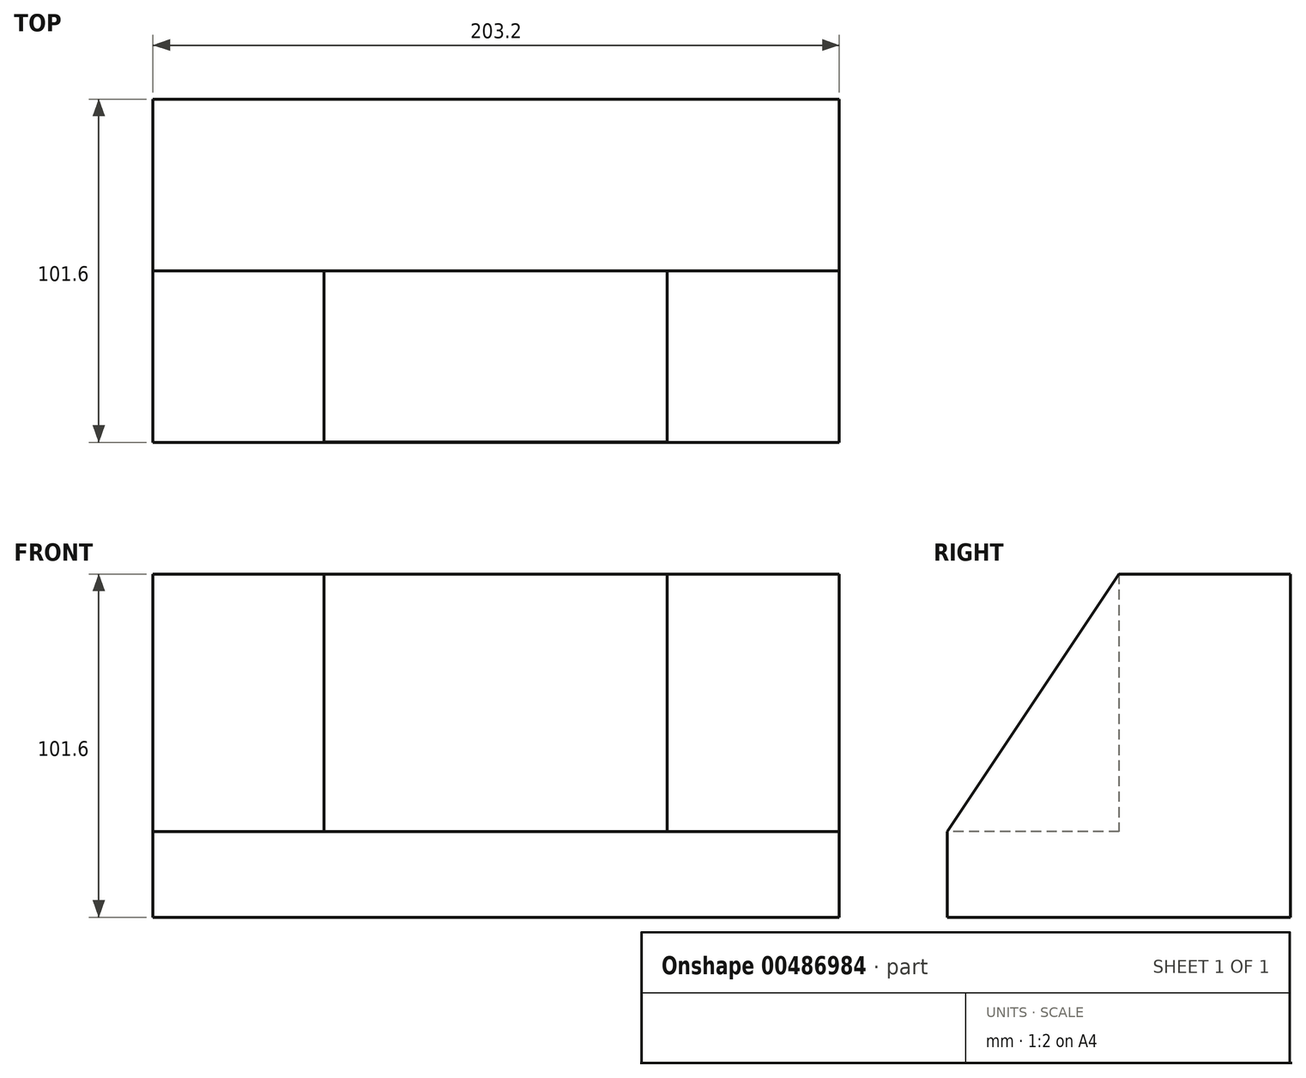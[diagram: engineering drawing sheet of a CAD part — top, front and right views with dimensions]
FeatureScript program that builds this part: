
annotation { "Feature Type Name" : "Feature", "Feature Type Description" : "" }
export const myFeature = defineFeature(function(context is Context, id is Id, definition is map)
    precondition{}
    {
        {
            var Q0;
            Q0=qCreatedBy(makeId("Front.planeOp"),FACE);
            var sketch = newSketch(context, id + "F0", { "sketchPlane" : qUnion([Q0])});
            skLineSegment(sketch, "E0.bottom", {"start": v(-109.3, 35.82) * mm, "end": v(93.9, 35.82) * mm});
            skLineSegment(sketch, "E0.top", {"start": v(-109.3, -65.78) * mm, "end": v(93.9, -65.78) * mm});
            skLineSegment(sketch, "E0.left", {"start": v(-109.3, 35.82) * mm, "end": v(-109.3, -65.78) * mm});
            skLineSegment(sketch, "E0.right", {"start": v(93.9, 35.82) * mm, "end": v(93.9, -65.78) * mm});
            skSolve(sketch);
        }
        {
            var Q0;
            Q0 = qSketchRegion(id + "F0", true);
            extrude(context, id + "F1", {"entities" : qUnion([Q0]), "depth" : 101.6 * mm});
        }
        {
            var Q0;
            Q0=makeQuery(id+"F1.opExtrude","CAP_FACE",FACE,{"disambiguationData":[OSD([sQuery(id+"F0.wireOp",EDGE,"E0.bottom"),sQuery(id+"F0.wireOp",EDGE,"E0.top"),sQuery(id+"F0.wireOp",EDGE,"E0.left"),sQuery(id+"F0.wireOp",EDGE,"E0.right")])],"isStart":false});
            var sketch = newSketch(context, id + "F2", { "sketchPlane" : qUnion([Q0])});
            skLineSegment(sketch, "E1", {"start": v(-109.3, 35.82) * mm, "end": v(-58.63, 35.82) * mm});
            skLineSegment(sketch, "E2.bottom", {"start": v(-58.63, 35.82) * mm, "end": v(42.97, 35.82) * mm});
            skLineSegment(sketch, "E2.top", {"start": v(-58.63, -40.38) * mm, "end": v(42.97, -40.38) * mm});
            skLineSegment(sketch, "E2.left", {"start": v(-58.63, 35.82) * mm, "end": v(-58.63, -40.38) * mm});
            skLineSegment(sketch, "E2.right", {"start": v(42.97, 35.82) * mm, "end": v(42.97, -40.38) * mm});
            skSolve(sketch);
        }
        {
            var Q0;
            Q0 = qSketchRegion(id + "F2", true);
            extrude(context, id + "F3", {"entities" : qUnion([Q0]), "operationType" : NewBodyOperationType.REMOVE, "oppositeDirection" : true, "depth" : 50.8 * mm});
        }
        {
            var Q0;
            Q0=makeQuery(id+"F1.opExtrude","SWEPT_FACE",FACE,{"disambiguationData":[OSD([sQuery(id+"F0.wireOp",EDGE,"E0.left")])]});
            var sketch = newSketch(context, id + "F4", { "sketchPlane" : qUnion([Q0])});
            skLineSegment(sketch, "E3", {"start": v(101.6, -65.78) * mm, "end": v(101.6, -40.38) * mm});
            skLineSegment(sketch, "E4", {"start": v(101.6, -40.38) * mm, "end": v(101.6, 35.82) * mm});
            skLineSegment(sketch, "E5", {"start": v(101.6, 35.82) * mm, "end": v(50.8, 35.82) * mm});
            skLineSegment(sketch, "E6", {"start": v(50.8, 35.82) * mm, "end": v(101.6, -40.38) * mm});
            skSolve(sketch);
        }
        {
            var Q0;
            Q0 = qSketchRegion(id + "F4", true);
            extrude(context, id + "F5", {"entities" : qUnion([Q0]), "operationType" : NewBodyOperationType.REMOVE, "oppositeDirection" : true, "depth" : 50.8 * mm});
        }
        {
            var Q0;
            Q0=makeQuery(id+"F1.opExtrude","SWEPT_FACE",FACE,{"disambiguationData":[OSD([sQuery(id+"F0.wireOp",EDGE,"E0.right")])]});
            var sketch = newSketch(context, id + "F6", { "sketchPlane" : qUnion([Q0])});
            skLineSegment(sketch, "E7", {"start": v(-101.6, -65.78) * mm, "end": v(-101.6, -40.48) * mm});
            skLineSegment(sketch, "E8", {"start": v(-101.6, -40.48) * mm, "end": v(-101.6, 35.82) * mm});
            skLineSegment(sketch, "E9", {"start": v(-101.6, 35.82) * mm, "end": v(-50.8, 35.82) * mm});
            skLineSegment(sketch, "E10", {"start": v(-50.8, 35.82) * mm, "end": v(-101.6, -40.48) * mm});
            skSolve(sketch);
        }
        {
            var Q0;
            Q0 = qSketchRegion(id + "F6", true);
            extrude(context, id + "F7", {"entities" : qUnion([Q0]), "operationType" : NewBodyOperationType.REMOVE, "endBound" : BoundingType.UP_TO_NEXT, "oppositeDirection" : true, "depth" : 50.8 * mm});
        }
    });
